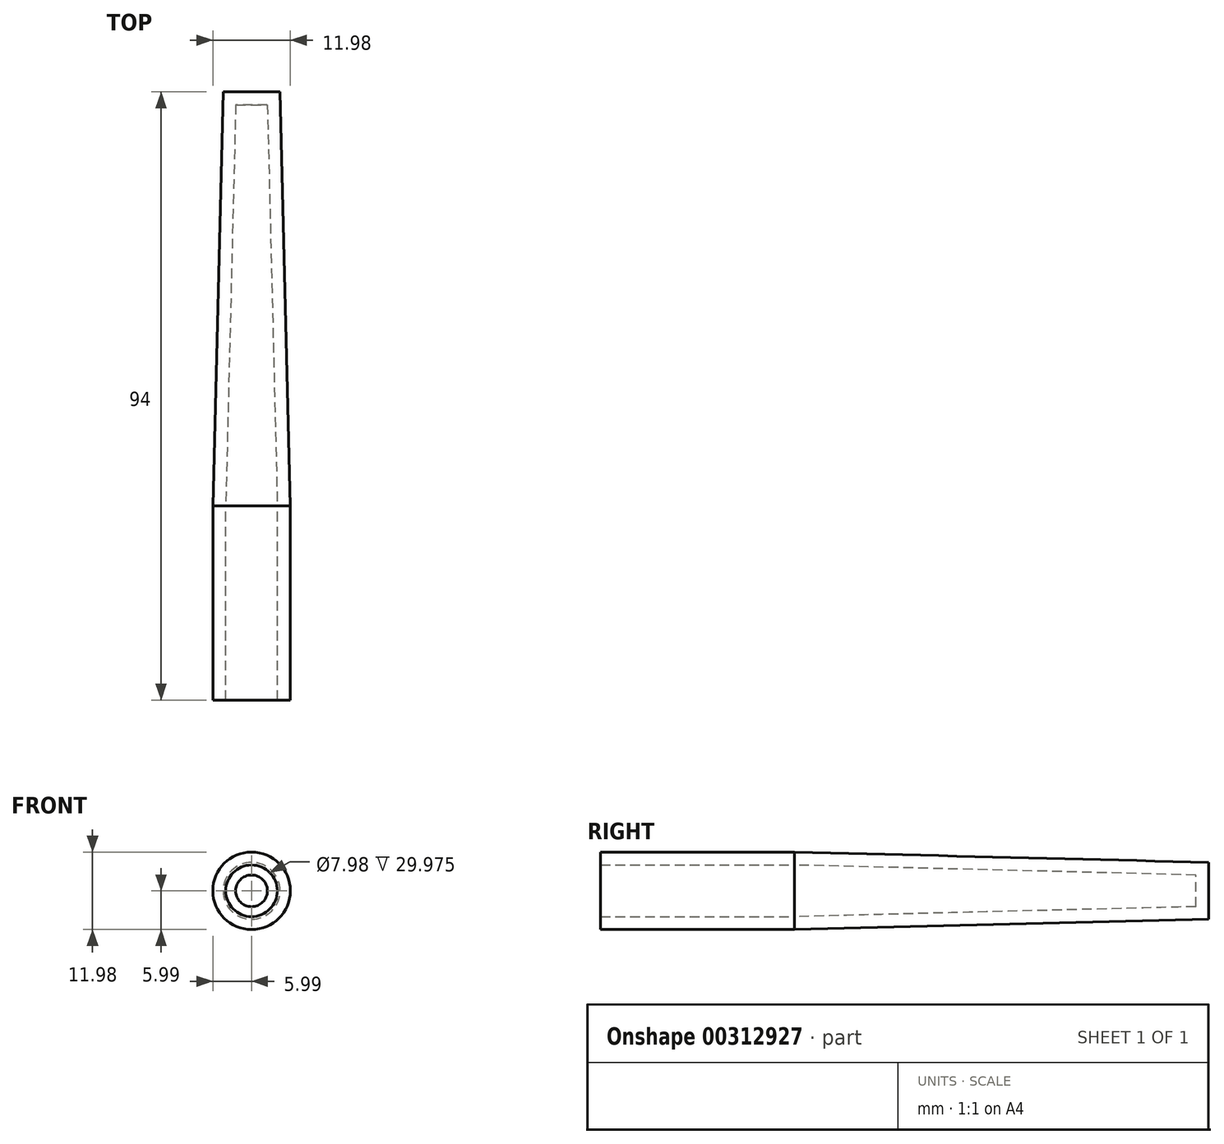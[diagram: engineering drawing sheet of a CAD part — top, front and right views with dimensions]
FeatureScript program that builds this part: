
annotation { "Feature Type Name" : "Feature", "Feature Type Description" : "" }
export const myFeature = defineFeature(function(context is Context, id is Id, definition is map)
    precondition{}
    {
        {
            var Q0;
            Q0=qCreatedBy(makeId("Right.planeOp"),FACE);
            var sketch = newSketch(context, id + "F0", { "sketchPlane" : qUnion([Q0])});
            skLineSegment(sketch, "E0", {"start": v(0, 5.99) * mm, "end": v(64, 4.4) * mm});
            skLineSegment(sketch, "E1", {"start": v(64, 4.4) * mm, "end": v(64, 0) * mm});
            skLineSegment(sketch, "E2", {"start": v(64, 0) * mm, "end": v(0, 0) * mm});
            skLineSegment(sketch, "E3", {"start": v(0, 5.99) * mm, "end": v(-30, 5.99) * mm});
            skLineSegment(sketch, "E4", {"start": v(-30, 5.99) * mm, "end": v(-30, 0) * mm});
            skLineSegment(sketch, "E5", {"start": v(-30, 0) * mm, "end": v(0, 0) * mm});
            skLineSegment(sketch, "E6", {"start": v(0, 8.9) * mm, "end": v(64, 7.3) * mm, "construction": true});
            skSolve(sketch);
        }
        {
            var Q0;
            Q0 = qSketchRegion(id + "F0", true);
            var Q1;
            Q1=sQuery(id+"F0.wireOp",EDGE,"E2");
            revolve(context, id + "F1", {"entities" : qUnion([Q0]), "axis" : qUnion([Q1]), "revolveType" : RevolveType.FULL});
        }
        {
            var Q0;
            Q0=makeQuery(id+"F1.opRevolve","SWEPT_FACE",FACE,{"disambiguationData":[OSD([sQuery(id+"F0.wireOp",EDGE,"E4")])]});
            shell(context, id + "F2", {"entities" : qUnion([Q0]), "thickness" : 2 * mm});
        }
    });
